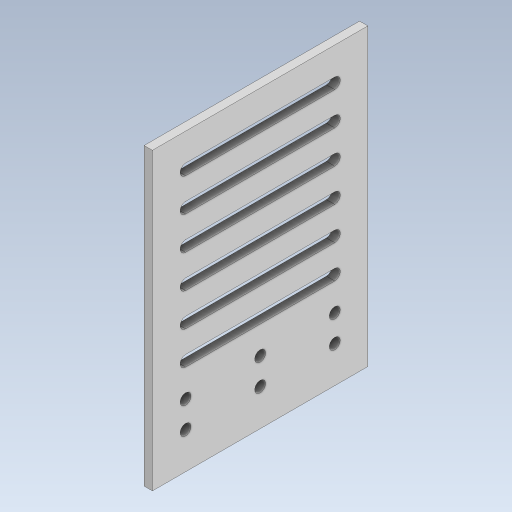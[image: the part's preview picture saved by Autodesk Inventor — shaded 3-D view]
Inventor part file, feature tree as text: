
AUTODESK INVENTOR PART (.ipt)
format: ipt  version: 2023.5 (Build 275446000, 446)  size: 367,104 bytes
history: native  units: mm
features: extrude x1, sketch x1
ambient origin geometry x8: Origin, YZ Plane, XZ Plane, XY Plane, X Axis, Y Axis, Z Axis, Center Point
bodies: Body1 (feature_tree)
feature tree (2):
  extrude  "Extrusion2"  Depth=3.3mm
  sketch  "Sketch1"  dims[d0=3.3mm d1=3.3mm d5=3.3mm d22=10.0mm d23=10.0mm d24=22.5mm d25=22.5mm d26=3.3mm d27=3.3mm d28=2.5mm d29=0.0mm d30=70.0mm d31=3.3mm d32=10.0mm d33=3.3mm d34=60.0mm d36=10.0mm d37=10.0mm d39=10.0mm]
